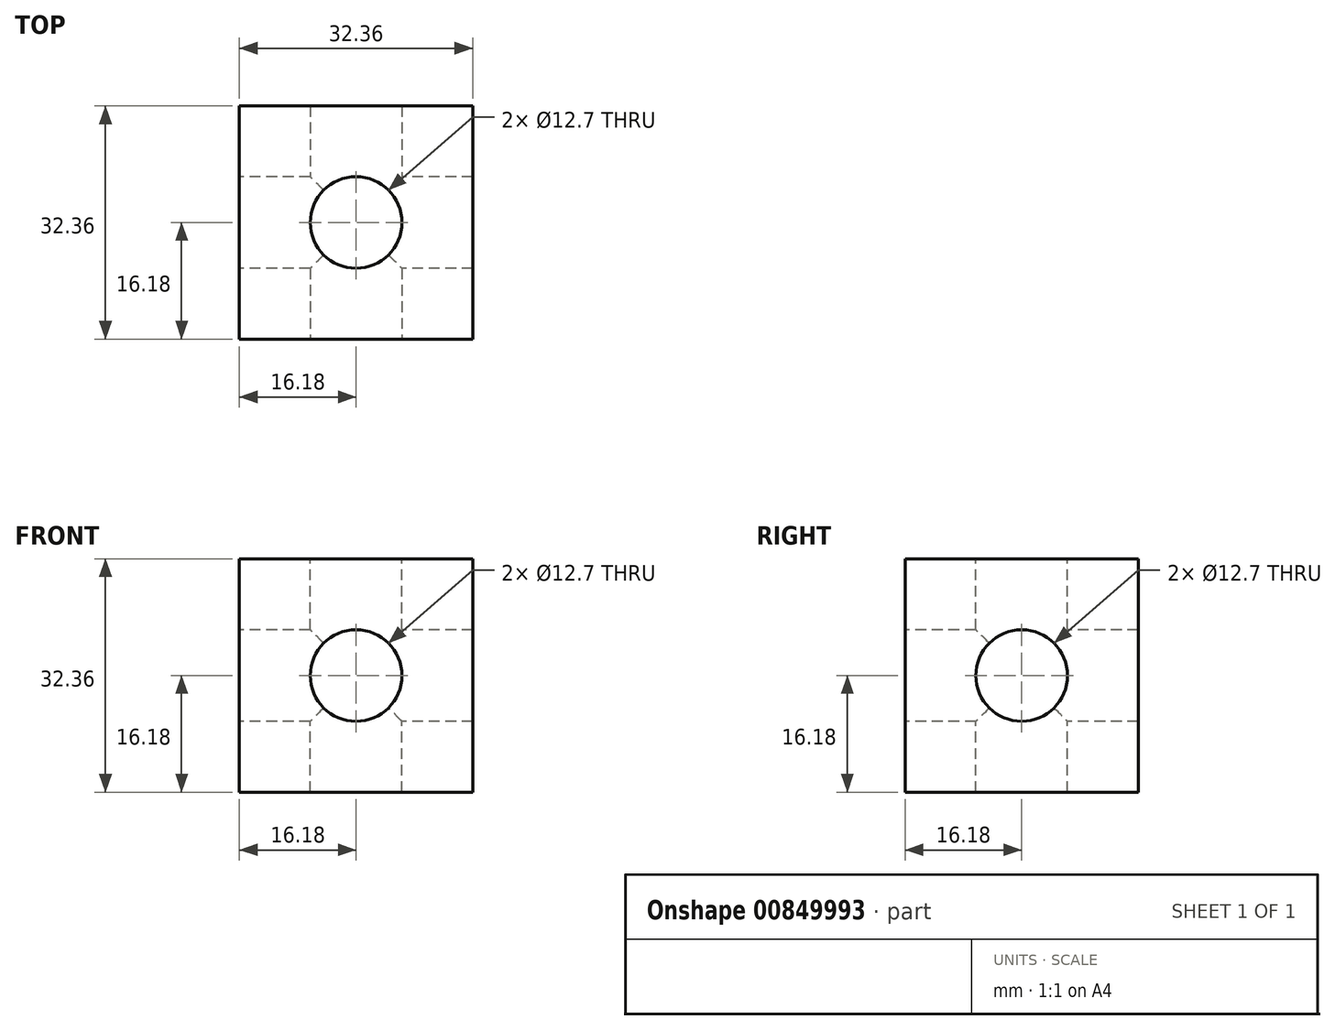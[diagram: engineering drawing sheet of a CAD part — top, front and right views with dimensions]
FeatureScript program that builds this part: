
annotation { "Feature Type Name" : "Feature", "Feature Type Description" : "" }
export const myFeature = defineFeature(function(context is Context, id is Id, definition is map)
    precondition{}
    {
        {
            var Q0;
            Q0=qCreatedBy(makeId("Top.planeOp"),FACE);
            var sketch = newSketch(context, id + "F0", { "sketchPlane" : qUnion([Q0])});
            skLineSegment(sketch, "E0.bottom", {"start": v(0, 0) * mm, "end": v(32.36, 0) * mm});
            skLineSegment(sketch, "E0.top", {"start": v(0, 32.36) * mm, "end": v(32.36, 32.36) * mm});
            skLineSegment(sketch, "E0.left", {"start": v(0, 0) * mm, "end": v(0, 32.36) * mm});
            skLineSegment(sketch, "E0.right", {"start": v(32.36, 0) * mm, "end": v(32.36, 32.36) * mm});
            skSolve(sketch);
        }
        {
            var Q0;
            Q0 = qSketchRegion(id + "F0", true);
            extrude(context, id + "F1", {"entities" : qUnion([Q0]), "depth" : 32.36 * mm, "offsetDistance" : 25.4 * mm});
        }
        {
            var Q0;
            Q0=makeQuery(id+"F1.opExtrude","CAP_FACE",FACE,{"disambiguationData":[OSD([sQuery(id+"F0.wireOp",EDGE,"E0.bottom"),sQuery(id+"F0.wireOp",EDGE,"E0.top"),sQuery(id+"F0.wireOp",EDGE,"E0.left"),sQuery(id+"F0.wireOp",EDGE,"E0.right")])],"isStart":false});
            var sketch = newSketch(context, id + "F2", { "sketchPlane" : qUnion([Q0])});
            skCircle(sketch, "E1", {"center": v(16.18, 16.18) * mm, "radius": 6.35 * mm});
            skPoint(sketch, "E1.centerSnap0", {"position": v(16.18, 32.36) * mm});
            skPoint(sketch, "E1.centerSnap1", {"position": v(32.36, 16.18) * mm});
            skSolve(sketch);
        }
        {
            var Q0;
            Q0 = qSketchRegion(id + "F2", true);
            extrude(context, id + "F3", {"entities" : qUnion([Q0]), "operationType" : NewBodyOperationType.REMOVE, "oppositeDirection" : true, "depth" : 44.45 * mm, "offsetDistance" : 25.4 * mm});
        }
        {
            var Q0;
            Q0=makeQuery(id+"F1.opExtrude","SWEPT_FACE",FACE,{"disambiguationData":[OSD([sQuery(id+"F0.wireOp",EDGE,"E0.bottom")])]});
            var sketch = newSketch(context, id + "F4", { "sketchPlane" : qUnion([Q0])});
            skCircle(sketch, "E2", {"center": v(16.18, 16.18) * mm, "radius": 6.35 * mm});
            skPoint(sketch, "E2.centerSnap0", {"position": v(32.36, 16.18) * mm});
            skPoint(sketch, "E2.centerSnap1", {"position": v(16.18, 32.36) * mm});
            skSolve(sketch);
        }
        {
            var Q0;
            Q0 = qSketchRegion(id + "F4", true);
            extrude(context, id + "F5", {"entities" : qUnion([Q0]), "operationType" : NewBodyOperationType.REMOVE, "oppositeDirection" : true, "depth" : 44.45 * mm, "offsetDistance" : 25.4 * mm});
        }
        {
            var Q0;
            Q0=makeQuery(id+"F1.opExtrude","SWEPT_FACE",FACE,{"disambiguationData":[OSD([sQuery(id+"F0.wireOp",EDGE,"E0.left")])]});
            var sketch = newSketch(context, id + "F6", { "sketchPlane" : qUnion([Q0])});
            skCircle(sketch, "E3", {"center": v(-16.18, 16.18) * mm, "radius": 6.35 * mm});
            skPoint(sketch, "E3.centerSnap0", {"position": v(0, 16.18) * mm});
            skPoint(sketch, "E3.centerSnap1", {"position": v(-16.18, 32.36) * mm});
            skSolve(sketch);
        }
        {
            var Q0;
            Q0 = qSketchRegion(id + "F6", true);
            extrude(context, id + "F7", {"entities" : qUnion([Q0]), "operationType" : NewBodyOperationType.REMOVE, "oppositeDirection" : true, "depth" : 44.45 * mm, "offsetDistance" : 25.4 * mm});
        }
    });
